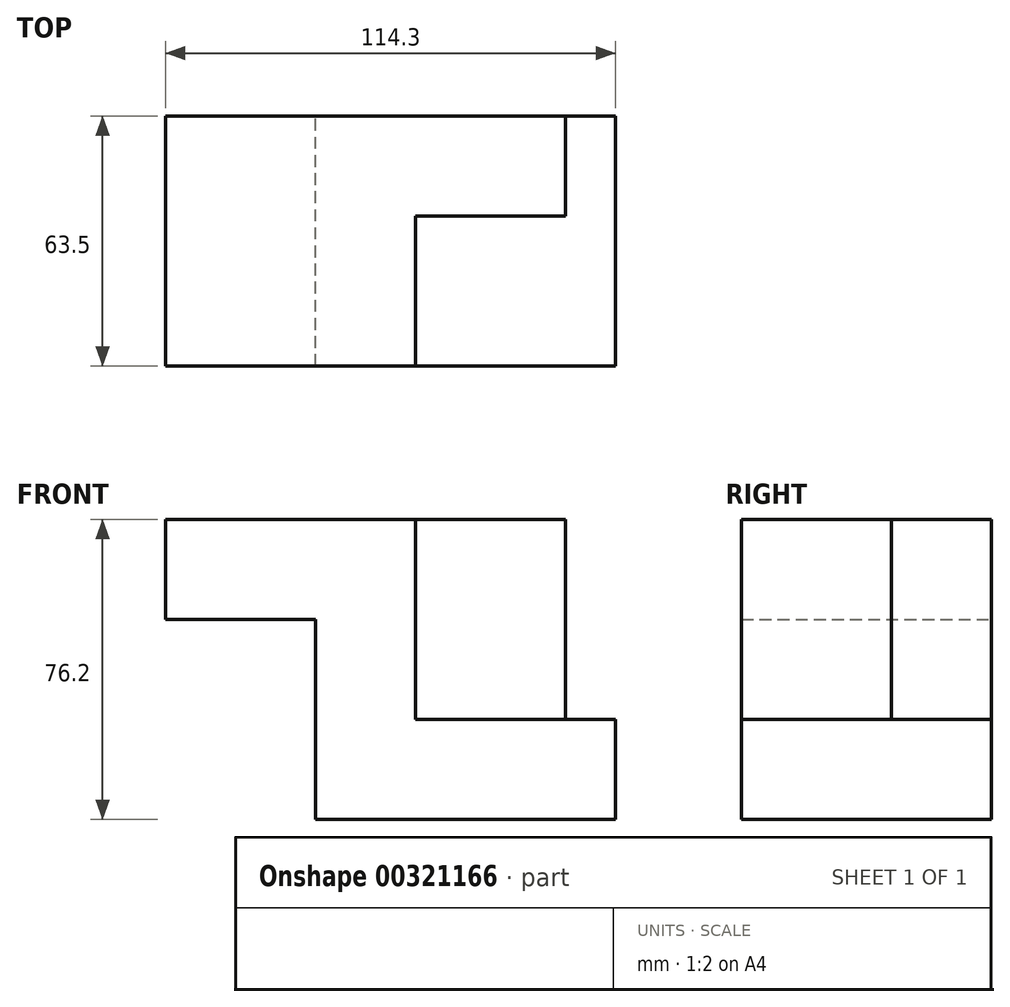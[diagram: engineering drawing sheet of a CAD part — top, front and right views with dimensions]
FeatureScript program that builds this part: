
annotation { "Feature Type Name" : "Feature", "Feature Type Description" : "" }
export const myFeature = defineFeature(function(context is Context, id is Id, definition is map)
    precondition{}
    {
        {
            var Q0;
            Q0=qCreatedBy(makeId("Front.planeOp"),FACE);
            var sketch = newSketch(context, id + "F0", { "sketchPlane" : qUnion([Q0])});
            skLineSegment(sketch, "E0", {"start": v(-81.44, 61.12) * mm, "end": v(-17.94, 61.12) * mm});
            skLineSegment(sketch, "E1", {"start": v(-17.94, 61.12) * mm, "end": v(-17.94, 10.32) * mm});
            skLineSegment(sketch, "E2", {"start": v(-17.94, 10.32) * mm, "end": v(32.86, 10.32) * mm});
            skLineSegment(sketch, "E3", {"start": v(32.86, 10.32) * mm, "end": v(32.86, -15.08) * mm});
            skLineSegment(sketch, "E4", {"start": v(-81.44, 61.12) * mm, "end": v(-81.44, 35.72) * mm});
            skLineSegment(sketch, "E5", {"start": v(-81.44, 35.72) * mm, "end": v(-43.34, 35.72) * mm});
            skLineSegment(sketch, "E6", {"start": v(-43.34, 35.72) * mm, "end": v(-43.34, -15.08) * mm});
            skLineSegment(sketch, "E7", {"start": v(32.86, -15.08) * mm, "end": v(-43.34, -15.08) * mm});
            skSolve(sketch);
        }
        {
            var Q0;
            Q0=makeQuery(id+"F0.imprint","IMPRINT",FACE,{"disambiguationData":[TD([[makeQuery(id+"F0.imprint","IMPRINT",EDGE,{"derivedFrom":sQuery(id+"F0.wireOp",EDGE,"E0")}),-1.0]])]});
            extrude(context, id + "F1", {"entities" : qUnion([Q0]), "depth" : 63.5 * mm});
        }
        {
            var Q0;
            Q0=makeQuery(id+"F1.opExtrude","SWEPT_FACE",FACE,{"disambiguationData":[OSD([sQuery(id+"F0.wireOp",EDGE,"E2")])]});
            var sketch = newSketch(context, id + "F2", { "sketchPlane" : qUnion([Q0])});
            skLineSegment(sketch, "E8.bottom", {"start": v(-17.94, -25.4) * mm, "end": v(20.16, -25.4) * mm});
            skLineSegment(sketch, "E9", {"start": v(20.16, -25.4) * mm, "end": v(20.16, 0) * mm});
            skSolve(sketch);
        }
        {
            var Q0;
            Q0 = qSketchRegion(id + "F2", true);
            var Q1;
            {var subQ0=sQuery(id+"F2.wireOp",EDGE,"E8.bottom");Q1=makeQuery(id+"F2.imprint","IMPRINT",FACE,{"disambiguationData":[TD([[makeQuery(id+"F2.imprint","IMPRINT",EDGE,{"derivedFrom":subQ0}),1.0]])]});}
            var Q2;
            Q2=makeQuery(id+"F1.opExtrude","SWEPT_FACE",FACE,{"disambiguationData":[OSD([sQuery(id+"F0.wireOp",EDGE,"E0")])]});
            extrude(context, id + "F3", {"entities" : qUnion([Q0, Q1]), "operationType" : NewBodyOperationType.ADD, "endBoundEntityFace" : qUnion([Q2]), "depth" : 50.8 * mm});
        }
    });
